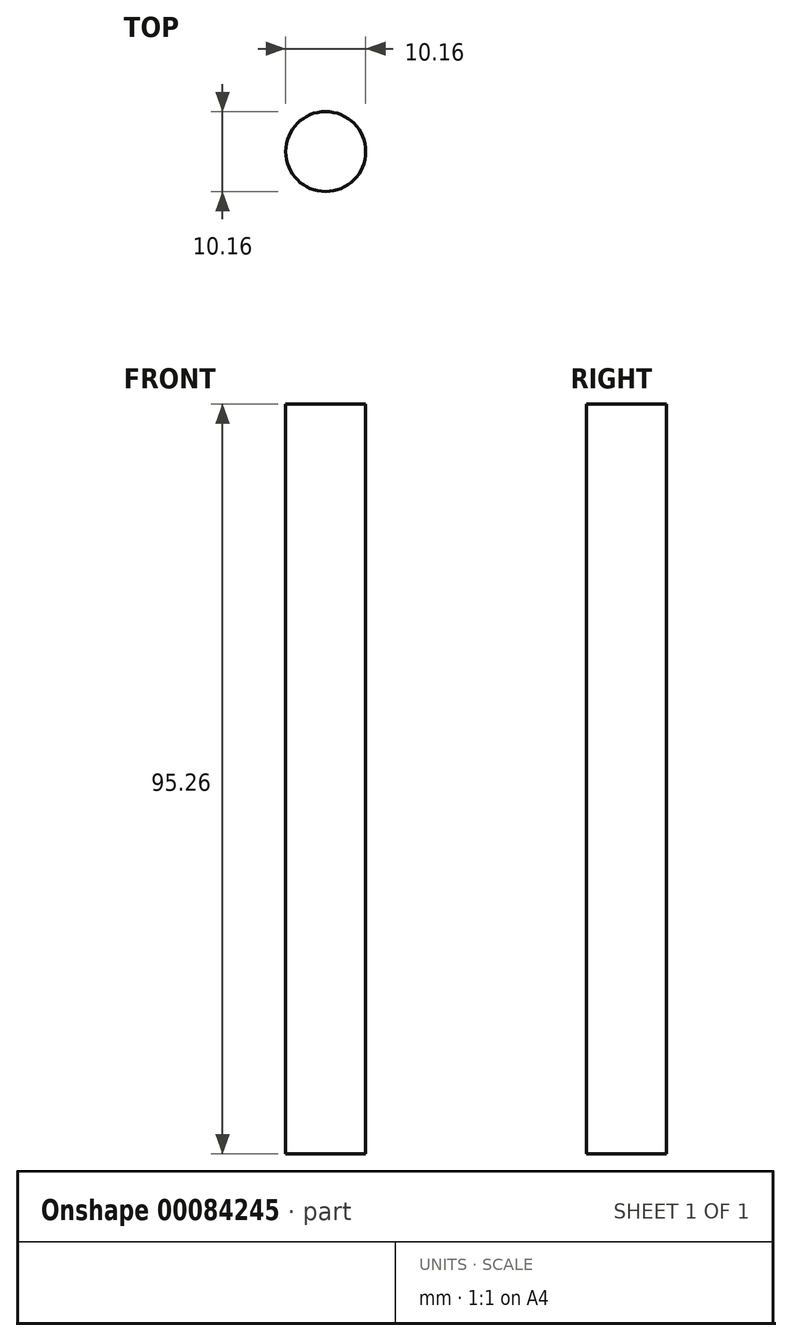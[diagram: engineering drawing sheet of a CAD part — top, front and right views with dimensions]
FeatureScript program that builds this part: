
annotation { "Feature Type Name" : "Feature", "Feature Type Description" : "" }
export const myFeature = defineFeature(function(context is Context, id is Id, definition is map)
    precondition{}
    {
        {
            var Q0;
            Q0=qCreatedBy(makeId("Top.planeOp"),FACE);
            var sketch = newSketch(context, id + "F0", { "sketchPlane" : qUnion([Q0])});
            skCircle(sketch, "E0", {"center": v(0, 0) * mm, "radius": 5.08 * mm});
            skSolve(sketch);
        }
        {
            var Q0;
            Q0 = qSketchRegion(id + "F0", true);
            extrude(context, id + "F1", {"entities" : qUnion([Q0]), "endBound" : BoundingType.SYMMETRIC, "depth" : 95.25 * mm});
        }
    });
